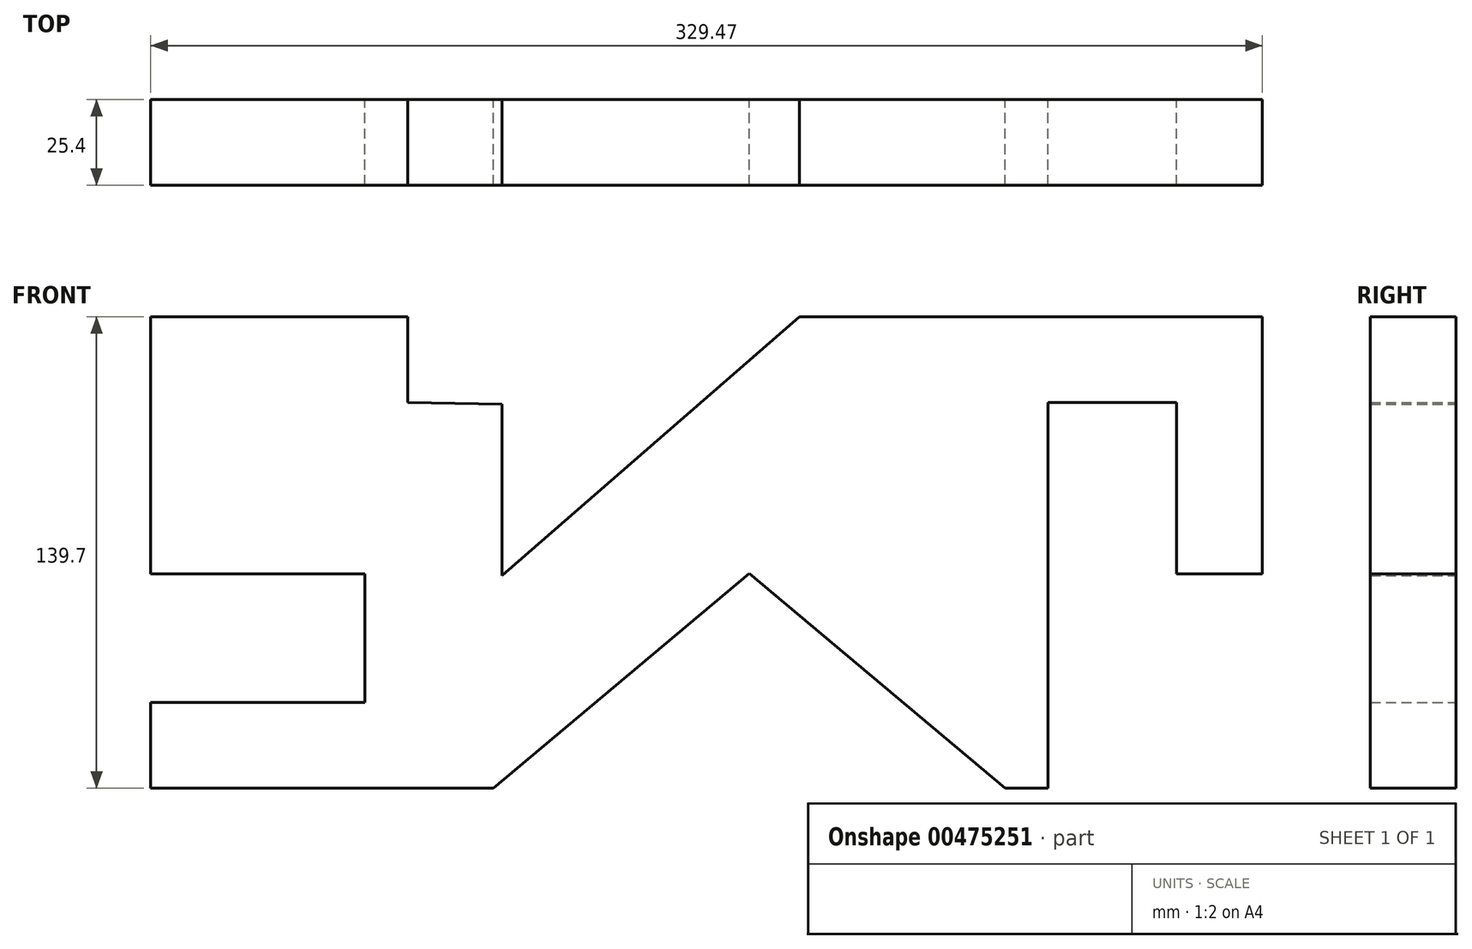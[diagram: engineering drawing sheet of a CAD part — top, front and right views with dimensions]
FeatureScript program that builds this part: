
annotation { "Feature Type Name" : "Feature", "Feature Type Description" : "" }
export const myFeature = defineFeature(function(context is Context, id is Id, definition is map)
    precondition{}
    {
        {
            var Q0;
            Q0=qCreatedBy(makeId("Front.planeOp"),FACE);
            var sketch = newSketch(context, id + "F0", { "sketchPlane" : qUnion([Q0])});
            skLineSegment(sketch, "E0", {"start": v(-86.71, 69.41) * mm, "end": v(-86.71, -6.79) * mm});
            skLineSegment(sketch, "E1", {"start": v(-86.71, -6.79) * mm, "end": v(-23.21, -6.79) * mm});
            skLineSegment(sketch, "E2", {"start": v(-23.21, -6.79) * mm, "end": v(-23.21, -44.89) * mm});
            skLineSegment(sketch, "E3", {"start": v(-23.21, -44.89) * mm, "end": v(-86.71, -44.89) * mm});
            skLineSegment(sketch, "E4", {"start": v(-86.71, -44.89) * mm, "end": v(-86.71, -70.29) * mm});
            skLineSegment(sketch, "E5", {"start": v(-86.71, -70.29) * mm, "end": v(14.89, -70.29) * mm});
            skLineSegment(sketch, "E6", {"start": v(14.89, -70.29) * mm, "end": v(90.72, -6.65) * mm});
            skLineSegment(sketch, "E7", {"start": v(14.89, -70.29) * mm, "end": v(39.59, -70.29) * mm});
            skLineSegment(sketch, "E8", {"start": v(90.72, -6.65) * mm, "end": v(166.56, -70.29) * mm});
            skLineSegment(sketch, "E9", {"start": v(166.56, -70.29) * mm, "end": v(179.26, -70.29) * mm});
            skLineSegment(sketch, "E10", {"start": v(179.26, -70.29) * mm, "end": v(179.26, 44.01) * mm});
            skLineSegment(sketch, "E11", {"start": v(179.26, 44.01) * mm, "end": v(217.36, 44.01) * mm});
            skLineSegment(sketch, "E12", {"start": v(217.36, 44.01) * mm, "end": v(217.36, -6.79) * mm});
            skLineSegment(sketch, "E13", {"start": v(217.36, -6.79) * mm, "end": v(242.76, -6.79) * mm});
            skLineSegment(sketch, "E14", {"start": v(242.76, -6.79) * mm, "end": v(242.76, 69.41) * mm});
            skLineSegment(sketch, "E15", {"start": v(242.76, 69.41) * mm, "end": v(105.6, 69.41) * mm});
            skLineSegment(sketch, "E16", {"start": v(-86.71, 69.41) * mm, "end": v(-10.51, 69.41) * mm});
            skLineSegment(sketch, "E17", {"start": v(-10.51, 69.41) * mm, "end": v(-10.51, 44.01) * mm});
            skLineSegment(sketch, "E18", {"start": v(-10.51, 44.01) * mm, "end": v(17.42, 43.56) * mm});
            skLineSegment(sketch, "E19", {"start": v(17.42, 43.56) * mm, "end": v(17.42, -7.24) * mm});
            skLineSegment(sketch, "E20", {"start": v(17.42, -7.24) * mm, "end": v(105.6, 69.41) * mm});
            skSolve(sketch);
        }
        {
            var Q0;
            Q0=makeQuery(id+"F0.imprint","IMPRINT",FACE,{"disambiguationData":[TD([[makeQuery(id+"F0.imprint","IMPRINT",EDGE,{"derivedFrom":sQuery(id+"F0.wireOp",EDGE,"E0")}),1.0]])]});
            extrude(context, id + "F1", {"entities" : qUnion([Q0]), "depth" : 25.4 * mm});
        }
    });
